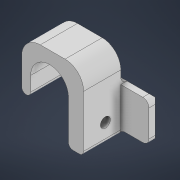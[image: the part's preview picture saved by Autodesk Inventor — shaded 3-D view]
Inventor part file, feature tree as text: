
AUTODESK INVENTOR PART (.ipt)
format: ipt  version: 2022 (Build 260153000, 153)  size: 197,120 bytes
history: native  units: mm
features: extrude x4, fillet x4, sketch x3, chamfer x1
ambient origin geometry x8: Origin, YZ Plane, XZ Plane, XY Plane, X Axis, Y Axis, Z Axis, Center Point
bodies: Solid1 (feature_tree)
feature tree (12):
  extrude  "Extrusion1"  Depth=18.0mm
  fillet  "Fillet1"  Radius=12.0mm
  fillet  "Fillet2"  Radius=4.0mm
  extrude  "Extrusion2"  Depth=1.45mm
  extrude  "Extrusion4"  Depth=2.0mm
  extrude  "Extrusion5"  TaperAngle=0.0deg  [1 undecoded]
  chamfer  "Chamfer1"  Distance=2.0mm
  fillet  "Fillet3"  Radius=3.2mm
  fillet  "Fillet4"  Radius=2.75mm
  sketch  "Sketch1"  dims[d0=12.2mm d1=18.0mm d2=12.0mm d3=0.0mm d4=4.0mm]
  sketch  "Sketch4"  dims[d5=6.0mm d6=1.45mm]
  sketch  "Sketch5"  dims[d10=10.0mm d11=0.0mm d16=5.0mm d17=0.0mm d18=2.0mm d19=3.2mm d20=2.75mm d21=2.5mm d22=0.0mm d23=2.0mm d24=14.0mm d25=3.0mm d26=0.0mm d27=1.0mm d28=2.0mm d29=45.0deg d30=2.0mm d31=2.0mm]
note: 1 required parameter value undecoded (feature->parameter linkage not recoverable at this tier; creation-order binding heuristic only, values carry confidence <= 0.55)
